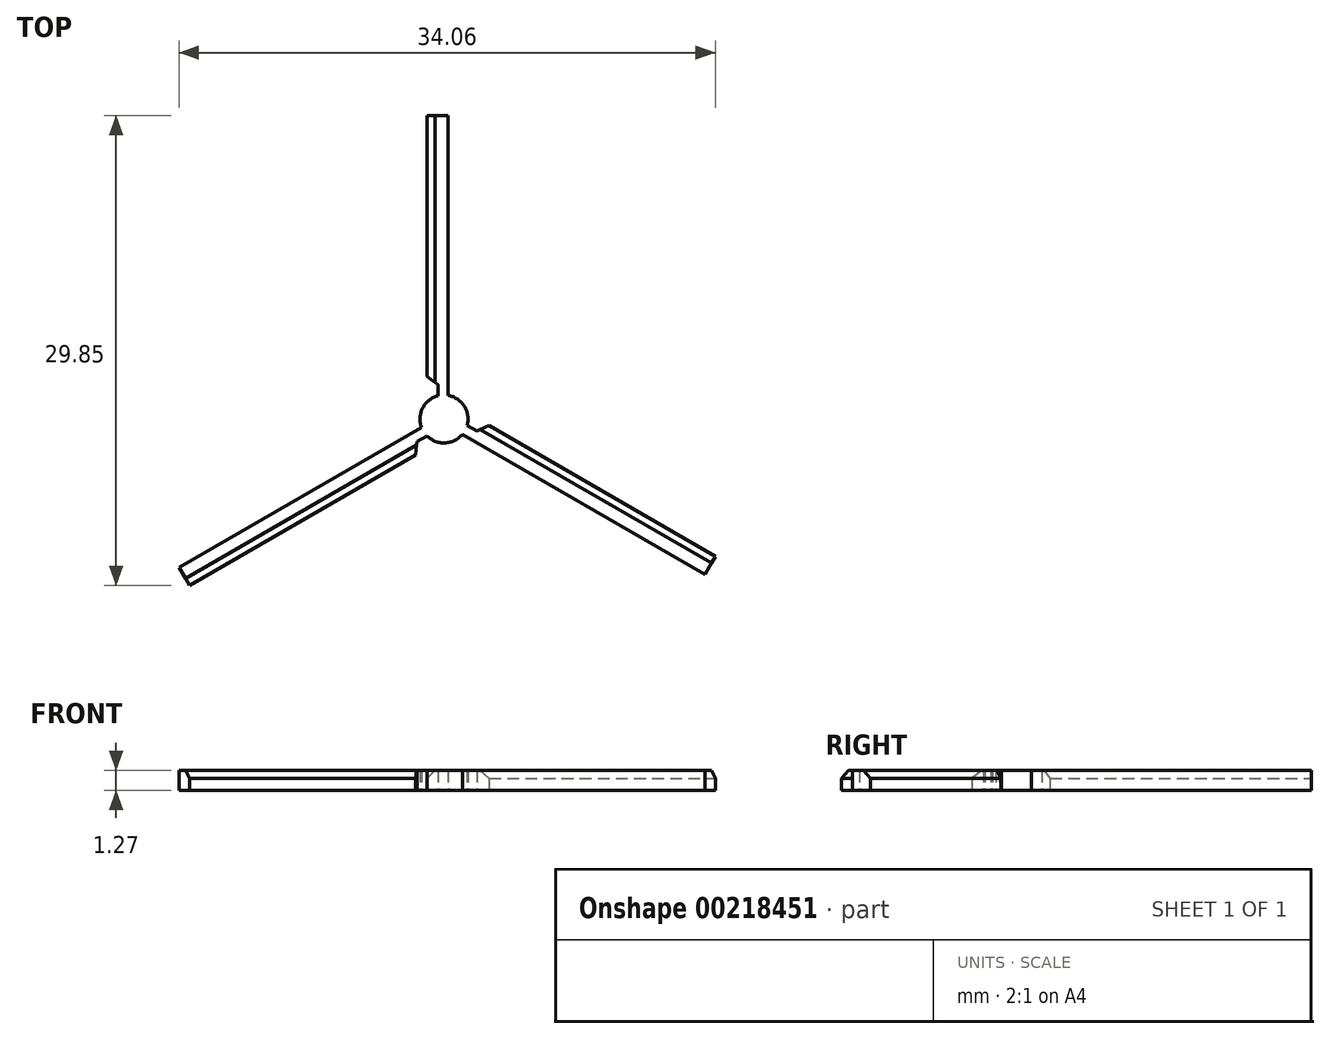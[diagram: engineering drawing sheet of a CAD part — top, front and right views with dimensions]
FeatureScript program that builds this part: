
annotation { "Feature Type Name" : "Feature", "Feature Type Description" : "" }
export const myFeature = defineFeature(function(context is Context, id is Id, definition is map)
    precondition{}
    {
        {
            var Q0;
            Q0=qCreatedBy(makeId("Top.planeOp"),FACE);
            var sketch = newSketch(context, id + "F0", { "sketchPlane" : qUnion([Q0])});
            skCircle(sketch, "E0", {"center": v(0, 0) * mm, "radius": 1.52 * mm});
            skLineSegment(sketch, "E1", {"start": v(0.26, 1.5) * mm, "end": v(0.26, 19.28) * mm});
            skLineSegment(sketch, "E2", {"start": v(0.26, 19.28) * mm, "end": v(-1.07, 19.28) * mm});
            skLineSegment(sketch, "E3", {"start": v(-1.07, 19.28) * mm, "end": v(-1.07, 2.7) * mm});
            skLineSegment(sketch, "E4", {"start": v(-1.07, 2.7) * mm, "end": v(-0.39, 2.2) * mm});
            skLineSegment(sketch, "E5", {"start": v(-0.39, 2.2) * mm, "end": v(-0.39, 1.47) * mm});
            skLineSegment(sketch, "E6.1.0", {"start": v(-1.43, -0.52) * mm, "end": v(-16.83, -9.41) * mm});
            skLineSegment(sketch, "E6.1.1", {"start": v(-16.83, -9.41) * mm, "end": v(-16.16, -10.57) * mm});
            skLineSegment(sketch, "E6.1.2", {"start": v(-16.16, -10.57) * mm, "end": v(-1.8, -2.27) * mm});
            skLineSegment(sketch, "E6.1.3", {"start": v(-1.8, -2.27) * mm, "end": v(-1.7, -1.43) * mm});
            skLineSegment(sketch, "E6.1.4", {"start": v(-1.7, -1.43) * mm, "end": v(-1.08, -1.07) * mm});
            skLineSegment(sketch, "E6.2.0", {"start": v(1.17, -0.98) * mm, "end": v(16.57, -9.87) * mm});
            skLineSegment(sketch, "E6.2.1", {"start": v(16.57, -9.87) * mm, "end": v(17.23, -8.72) * mm});
            skLineSegment(sketch, "E6.2.2", {"start": v(17.23, -8.72) * mm, "end": v(2.87, -0.42) * mm});
            skLineSegment(sketch, "E6.2.3", {"start": v(2.87, -0.42) * mm, "end": v(2.1, -0.76) * mm});
            skLineSegment(sketch, "E6.2.4", {"start": v(2.1, -0.76) * mm, "end": v(1.47, -0.4) * mm});
            skSolve(sketch);
        }
        {
            var Q0;
            {var subQ0=sQuery(id+"F0.wireOp",EDGE,"E0");var subQ5=makeQuery(id+"F0.imprint","INTERSECT",VERTEX,{"derivedFrom":[subQ0,sQuery(id+"F0.wireOp",EDGE,"E1")]});Q0=makeQuery(id+"F0.imprint","IMPRINT",FACE,{"disambiguationData":[TD([[makeQuery(id+"F0.imprint","IMPRINT",EDGE,{"disambiguationData":[TD([[subQ5,-1.0]])],"derivedFrom":subQ0}),1.0]])]});}
            var Q1;
            {var subQ0=sQuery(id+"F0.wireOp",EDGE,"E1");Q1=makeQuery(id+"F0.imprint","IMPRINT",FACE,{"disambiguationData":[TD([[makeQuery(id+"F0.imprint","IMPRINT",EDGE,{"derivedFrom":subQ0}),1.0]])]});}
            var Q2;
            {var subQ0=sQuery(id+"F0.wireOp",EDGE,"E6.2.0");Q2=makeQuery(id+"F0.imprint","IMPRINT",FACE,{"disambiguationData":[TD([[makeQuery(id+"F0.imprint","IMPRINT",EDGE,{"derivedFrom":subQ0}),1.0]])]});}
            var Q3;
            {var subQ0=sQuery(id+"F0.wireOp",EDGE,"E6.1.0");Q3=makeQuery(id+"F0.imprint","IMPRINT",FACE,{"disambiguationData":[TD([[makeQuery(id+"F0.imprint","IMPRINT",EDGE,{"derivedFrom":subQ0}),1.0]])]});}
            extrude(context, id + "F1", {"entities" : qUnion([Q0, Q1, Q2, Q3]), "depth" : 1.27 * mm});
        }
        {
            var Q0;
            Q0=makeQuery(id+"F1.opExtrude","CAP_EDGE",EDGE,{"disambiguationData":[OSD([sQuery(id+"F0.wireOp",EDGE,"E3")])],"isStart":false});
            var Q1;
            Q1=makeQuery(id+"F1.opExtrude","CAP_EDGE",EDGE,{"disambiguationData":[OSD([sQuery(id+"F0.wireOp",EDGE,"E6.1.2")])],"isStart":false});
            var Q2;
            Q2=makeQuery(id+"F1.opExtrude","CAP_EDGE",EDGE,{"disambiguationData":[OSD([sQuery(id+"F0.wireOp",EDGE,"E6.2.2")])],"isStart":false});
            chamfer(context, id + "F2", {"entities" : qUnion([Q0, Q1, Q2]), "width" : 0.5 * mm, "tangentPropagation" : true});
        }
    });
